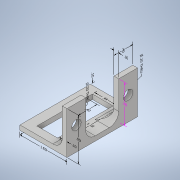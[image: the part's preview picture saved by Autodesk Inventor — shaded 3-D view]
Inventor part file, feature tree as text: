
AUTODESK INVENTOR PART (.ipt)
format: ipt  version: 2020 (Build 240168000, 168)  size: 184,320 bytes
history: native  units: in
note: dims shown in document units (in); Inventor stores cm internally (conversion verified against a paired STEP export)
features: sketch x5, extrude x3, hole x2, fillet x1
ambient origin geometry x8: Origin, YZ Plane, XZ Plane, XY Plane, X Axis, Y Axis, Z Axis, Center Point
bodies: Solid1 (feature_tree)
feature tree (11):
  extrude  "Extrusion1"  Depth=1.5in
  extrude  "Extrusion2"  Depth=0.2in
  extrude  "Extrusion3"  Depth=0.2in
  hole  "Hole1"  [1 undecoded]
  hole  "Hole2"  [1 undecoded]
  fillet  "Fillet1"  Radius=0.4in
  sketch  "Sketch1"  dims[d0=1.0in d1=1.5in]
  sketch  "Sketch3"  dims[d2=0.1in d3=0.0in d7=0.2in]
  sketch  "Sketch4"  dims[d8=0.16in d9=0.2in]
  sketch  "Sketch5"  dims[d10=0.16in d11=0.44in]
  sketch  "Sketch6"  dims[d12=0.1in d13=0.0in d14=0.1in d15=0.4in d16=0.1in d17=0.4in d18=0.8in d19=0.0in d20=0.4in d21=0.2in d22=0.75in d23=0.375in d24=0.25in d25=0.5635in d26=1.0in d27=0.8108in d28=0.4in d29=0.2in d30=0.75in d31=0.375in d32=0.25in d33=0.5635in d34=1.0in d35=0.8108in d76=0.2in d39=0.3313in d40=0.2404in d41=1.18in d42=0.0291in d43=0.368in d44=0.44in d45=0.1913in d46=0.2744in d47=1.5in d48=0.3605in d49=0.3601in d50=0.1in d51=0.0149in d52=0.1949in d53=1.0in d54=1.3283in d56=1.3744in d58=0.0808in d59=0.0305in d60=0.1in d61=0.2024in d62=0.3795in d63=0.9in d64=0.186in d65=0.2159in d66=0.4in d67=0.1931in d68=0.0746in d69=0.4in d70=0.1349in d71=0.1348in d72=0.8in d73=0.1747in d74=0.1613in d75=0.1in]
note: 2 required parameter values undecoded (feature->parameter linkage not recoverable at this tier; creation-order binding heuristic only, values carry confidence <= 0.55)
